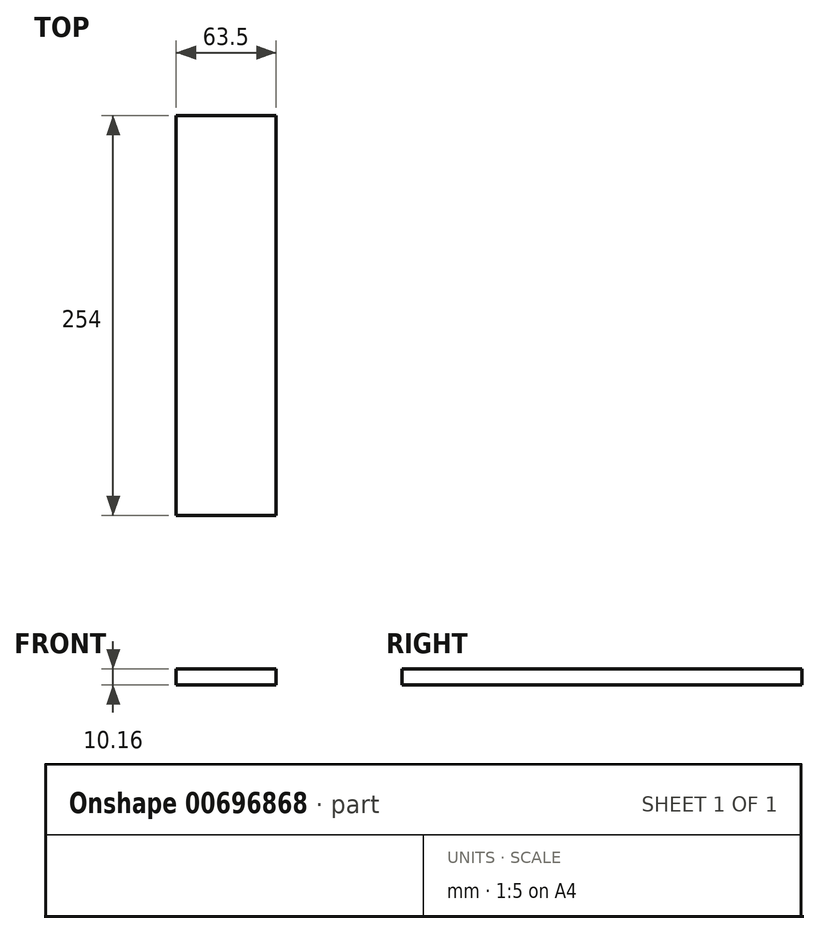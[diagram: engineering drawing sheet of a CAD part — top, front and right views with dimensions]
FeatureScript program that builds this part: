
annotation { "Feature Type Name" : "Feature", "Feature Type Description" : "" }
export const myFeature = defineFeature(function(context is Context, id is Id, definition is map)
    precondition{}
    {
        {
            var Q0;
            Q0=qCreatedBy(makeId("Top.planeOp"),FACE);
            var sketch = newSketch(context, id + "F0", { "sketchPlane" : qUnion([Q0])});
            skLineSegment(sketch, "E0.bottom", {"start": v(-31.75, 127) * mm, "end": v(31.75, 127) * mm});
            skLineSegment(sketch, "E0.top", {"start": v(-31.75, -127) * mm, "end": v(31.75, -127) * mm});
            skLineSegment(sketch, "E0.left", {"start": v(-31.75, 127) * mm, "end": v(-31.75, -127) * mm});
            skLineSegment(sketch, "E0.right", {"start": v(31.75, 127) * mm, "end": v(31.75, -127) * mm});
            skPoint(sketch, "E0.middle", {"position": v(0, 0) * mm});
            skSolve(sketch);
        }
        {
            var Q0;
            Q0 = qSketchRegion(id + "F0", true);
            extrude(context, id + "F1", {"entities" : qUnion([Q0]), "endBound" : BoundingType.SYMMETRIC, "oppositeDirection" : true, "depth" : 5.08 * mm, "offsetDistance" : 25.4 * mm});
        }
        {
            var Q0;
            Q0=makeQuery(id+"F1.opExtrude","CAP_FACE",FACE,{"disambiguationData":[OSD([sQuery(id+"F0.wireOp",EDGE,"E0.bottom"),sQuery(id+"F0.wireOp",EDGE,"E0.top"),sQuery(id+"F0.wireOp",EDGE,"E0.left"),sQuery(id+"F0.wireOp",EDGE,"E0.right")])],"isStart":true});
            var Q1;
            Q1=sQuery(id+"FKnkB7EDtI1W45k_1.wireOp",EDGE,"Ii4EiKg9-hCxk-hFll-KlSj-cyJWl4GbV4jY.bottom");
            var Q2;
            Q2=sQuery(id+"FKnkB7EDtI1W45k_1.wireOp",EDGE,"Ii4EiKg9-hCxk-hFll-KlSj-cyJWl4GbV4jY.top");
            var Q3;
            Q3=sQuery(id+"FKnkB7EDtI1W45k_1.wireOp",EDGE,"Ii4EiKg9-hCxk-hFll-KlSj-cyJWl4GbV4jY.left");
            var Q4;
            Q4=sQuery(id+"FKnkB7EDtI1W45k_1.wireOp",EDGE,"Ii4EiKg9-hCxk-hFll-KlSj-cyJWl4GbV4jY.right");
            extrude(context, id + "F2", {"entities" : qUnion([Q0]), "operationType" : NewBodyOperationType.ADD, "surfaceEntities" : qUnion([Q1, Q2, Q3, Q4]), "depth" : 5.08 * mm, "offsetDistance" : 25.4 * mm});
        }
    });
